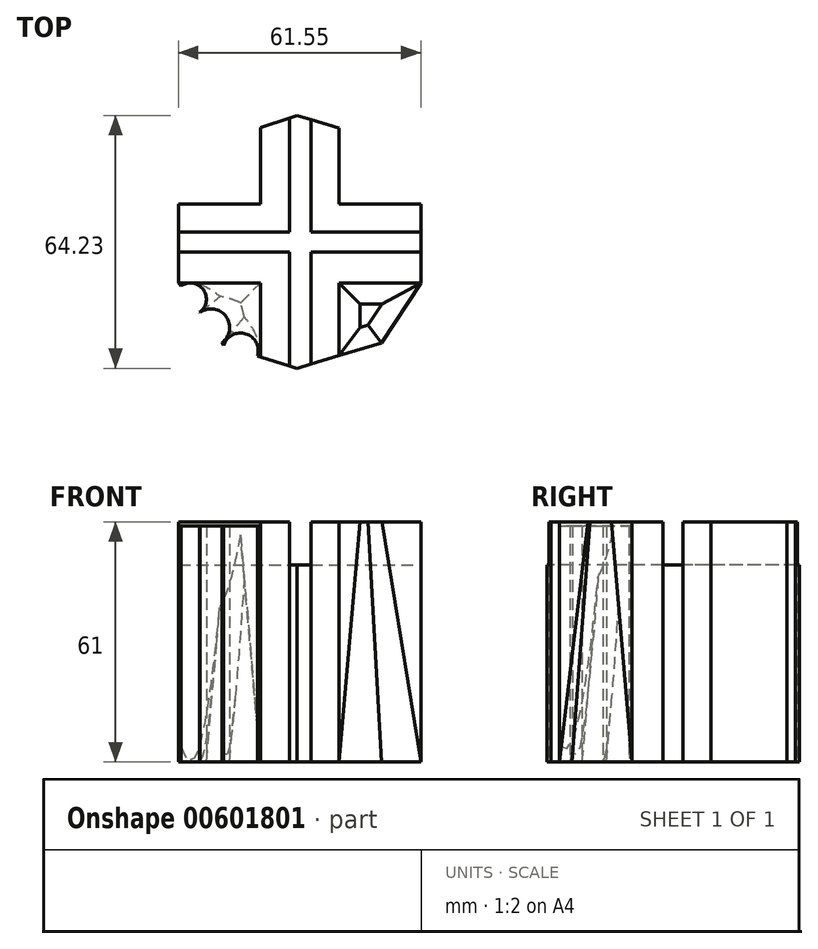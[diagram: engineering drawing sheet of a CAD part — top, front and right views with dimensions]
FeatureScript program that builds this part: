
annotation { "Feature Type Name" : "Feature", "Feature Type Description" : "" }
export const myFeature = defineFeature(function(context is Context, id is Id, definition is map)
    precondition{}
    {
        {
            var Q0;
            Q0=qCreatedBy(makeId("Top.planeOp"),FACE);
            var sketch = newSketch(context, id + "F0", { "sketchPlane" : qUnion([Q0])});
            skLineSegment(sketch, "E0.0", {"start": v(-30.78, -10.35) * mm, "end": v(-30.78, 9.65) * mm});
            skLineSegment(sketch, "E0.1", {"start": v(-30.78, 9.65) * mm, "end": v(-19.3, 26.03) * mm});
            skLineSegment(sketch, "E0.2", {"start": v(-19.3, 26.03) * mm, "end": v(-0.71, 32.18) * mm});
            skLineSegment(sketch, "E0.3", {"start": v(-0.71, 32.18) * mm, "end": v(18.71, 26.39) * mm});
            skLineSegment(sketch, "E0.4", {"start": v(18.71, 26.39) * mm, "end": v(30.77, 9.65) * mm});
            skLineSegment(sketch, "E0.5", {"start": v(30.77, 9.65) * mm, "end": v(30.77, -10.35) * mm});
            skLineSegment(sketch, "E0.6", {"start": v(30.77, -10.35) * mm, "end": v(20.71, -25.6) * mm});
            skLineSegment(sketch, "E0.7", {"start": v(20.71, -25.6) * mm, "end": v(-0.7, -32.05) * mm});
            skLineSegment(sketch, "E0.8", {"start": v(-0.7, -32.05) * mm, "end": v(-19.32, -26.2) * mm});
            skLineSegment(sketch, "E0.9", {"start": v(-19.32, -26.2) * mm, "end": v(-30.78, -10.35) * mm});
            skPoint(sketch, "E0.0.midPoint", {"position": v(-30.78, -0.35) * mm});
            skLineSegment(sketch, "E1", {"start": v(-30.78, 9.65) * mm, "end": v(30.77, 9.65) * mm});
            skLineSegment(sketch, "E2", {"start": v(-30.78, -10.35) * mm, "end": v(30.77, -10.35) * mm});
            skLineSegment(sketch, "E3", {"start": v(-10, 29.1) * mm, "end": v(-10, -29.12) * mm});
            skLineSegment(sketch, "E4", {"start": v(10, 28.98) * mm, "end": v(10, -28.83) * mm});
            skArc(sketch, "E5", {"start": v(-19.32, -26.2) * mm, "mid": v(-13.7, -23.27) * mm, "end": v(-10.77, -28.88) * mm});
            skLineSegment(sketch, "E6", {"start": v(-30.78, 2.54) * mm, "end": v(30.77, 2.54) * mm});
            skLineSegment(sketch, "E7", {"start": v(-2.54, 31.62) * mm, "end": v(-2.54, -31.47) * mm});
            skLineSegment(sketch, "E8", {"start": v(-30.78, -2.54) * mm, "end": v(30.77, -2.54) * mm});
            skLineSegment(sketch, "E9", {"start": v(2.82, 31.13) * mm, "end": v(2.82, -30.99) * mm});
            skArc(sketch, "E10", {"start": v(-25.37, -17.83) * mm, "mid": v(-18.72, -18.9) * mm, "end": v(-19.79, -25.54) * mm});
            skArc(sketch, "E11", {"start": v(-30.2, -11.16) * mm, "mid": v(-24.49, -12.08) * mm, "end": v(-25.4, -17.78) * mm});
            skLineSegment(sketch, "E12", {"start": v(0, 0) * mm, "end": v(-38.82, 0) * mm, "construction": true});
            skLineSegment(sketch, "E13", {"start": v(0, 0) * mm, "end": v(0, -35.82) * mm, "construction": true});
            skSolve(sketch);
        }
        {
            var Q0;
            {var subQ0=sQuery(id+"F0.wireOp",EDGE,"E6");var subQ1=sQuery(id+"F0.wireOp",EDGE,"E0.0");var subQ2=makeQuery(id+"F0.imprint","INTERSECT",VERTEX,{"derivedFrom":[subQ1,subQ0]});Q0=makeQuery(id+"F0.imprint","IMPRINT",FACE,{"disambiguationData":[TD([[makeQuery(id+"F0.imprint","IMPRINT",EDGE,{"disambiguationData":[TD([[subQ2,1.0]])],"derivedFrom":subQ1}),-1.0]])]});}
            var Q1;
            {var subQ0=sQuery(id+"F0.wireOp",EDGE,"E6");var subQ1=sQuery(id+"F0.wireOp",EDGE,"E4");var subQ2=makeQuery(id+"F0.imprint","INTERSECT",VERTEX,{"derivedFrom":[subQ1,subQ0]});Q1=makeQuery(id+"F0.imprint","IMPRINT",FACE,{"disambiguationData":[TD([[makeQuery(id+"F0.imprint","IMPRINT",EDGE,{"disambiguationData":[TD([[subQ2,-1.0]])],"derivedFrom":subQ1}),-1.0]])]});}
            var Q2;
            {var subQ0=sQuery(id+"F0.wireOp",EDGE,"E6");var subQ1=sQuery(id+"F0.wireOp",EDGE,"E3");var subQ2=makeQuery(id+"F0.imprint","INTERSECT",VERTEX,{"derivedFrom":[subQ1,subQ0]});Q2=makeQuery(id+"F0.imprint","IMPRINT",FACE,{"disambiguationData":[TD([[makeQuery(id+"F0.imprint","IMPRINT",EDGE,{"disambiguationData":[TD([[subQ2,-1.0]])],"derivedFrom":subQ1}),1.0]])]});}
            var Q3;
            {var subQ0=sQuery(id+"F0.wireOp",EDGE,"E6");var subQ1=sQuery(id+"F0.wireOp",EDGE,"E0.5");var subQ2=makeQuery(id+"F0.imprint","INTERSECT",VERTEX,{"derivedFrom":[subQ1,subQ0]});Q3=makeQuery(id+"F0.imprint","IMPRINT",FACE,{"disambiguationData":[TD([[makeQuery(id+"F0.imprint","IMPRINT",EDGE,{"disambiguationData":[TD([[subQ2,-1.0]])],"derivedFrom":subQ1}),-1.0]])]});}
            var Q4;
            {var subQ0=sQuery(id+"F0.wireOp",EDGE,"E7");var subQ1=sQuery(id+"F0.wireOp",EDGE,"E2");var subQ2=makeQuery(id+"F0.imprint","INTERSECT",VERTEX,{"derivedFrom":[subQ1,subQ0]});Q4=makeQuery(id+"F0.imprint","IMPRINT",FACE,{"disambiguationData":[TD([[makeQuery(id+"F0.imprint","IMPRINT",EDGE,{"disambiguationData":[TD([[subQ2,-1.0]])],"derivedFrom":subQ1}),1.0]])]});}
            var Q5;
            {var subQ1=sQuery(id+"F0.wireOp",EDGE,"E0.8");var subQ7=sQuery(id+"F0.wireOp",EDGE,"E0.7");var subQ8=makeQuery(id+"F0.imprint","INTERSECT",VERTEX,{"derivedFrom":[subQ7,subQ1]});Q5=makeQuery(id+"F0.imprint","IMPRINT",FACE,{"disambiguationData":[TD([[makeQuery(id+"F0.imprint","IMPRINT",EDGE,{"disambiguationData":[TD([[subQ8,1.0]])],"derivedFrom":subQ7}),-1.0]])]});}
            var Q6;
            {var subQ0=sQuery(id+"F0.wireOp",EDGE,"E7");var subQ1=sQuery(id+"F0.wireOp",EDGE,"E6");var subQ2=makeQuery(id+"F0.imprint","INTERSECT",VERTEX,{"derivedFrom":[subQ1,subQ0]});Q6=makeQuery(id+"F0.imprint","IMPRINT",FACE,{"disambiguationData":[TD([[makeQuery(id+"F0.imprint","IMPRINT",EDGE,{"disambiguationData":[TD([[subQ2,-1.0]])],"derivedFrom":subQ1}),-1.0]])]});}
            var Q7;
            {var subQ0=sQuery(id+"F0.wireOp",EDGE,"E7");var subQ1=sQuery(id+"F0.wireOp",EDGE,"E1");var subQ2=makeQuery(id+"F0.imprint","INTERSECT",VERTEX,{"derivedFrom":[subQ1,subQ0]});Q7=makeQuery(id+"F0.imprint","IMPRINT",FACE,{"disambiguationData":[TD([[makeQuery(id+"F0.imprint","IMPRINT",EDGE,{"disambiguationData":[TD([[subQ2,-1.0]])],"derivedFrom":subQ1}),-1.0]])]});}
            var Q8;
            {var subQ1=sQuery(id+"F0.wireOp",EDGE,"E0.2");var subQ7=sQuery(id+"F0.wireOp",EDGE,"E0.3");var subQ8=makeQuery(id+"F0.imprint","INTERSECT",VERTEX,{"derivedFrom":[subQ1,subQ7]});Q8=makeQuery(id+"F0.imprint","IMPRINT",FACE,{"disambiguationData":[TD([[makeQuery(id+"F0.imprint","IMPRINT",EDGE,{"disambiguationData":[TD([[subQ8,1.0]])],"derivedFrom":subQ1}),-1.0]])]});}
            extrude(context, id + "F1", {"entities" : qUnion([Q0, Q1, Q2, Q3, Q4, Q5, Q6, Q7, Q8]), "depth" : 50 * mm, "offsetDistance" : 25.4 * mm});
        }
        {
            var Q0;
            {var subQ0=sQuery(id+"F0.wireOp",EDGE,"E5");Q0=makeQuery(id+"F0.imprint","IMPRINT",FACE,{"disambiguationData":[TD([[makeQuery(id+"F0.imprint","IMPRINT",EDGE,{"derivedFrom":subQ0}),-1.0]])]});}
            var Q1;
            {var subQ0=sQuery(id+"F0.wireOp",EDGE,"8J1Gu1ok-NpBy-1UeC-TUCD-iMnJK34ZlI8X");Q1=makeQuery(id+"F0.imprint","IMPRINT",FACE,{"disambiguationData":[TD([[makeQuery(id+"F0.imprint","IMPRINT",EDGE,{"derivedFrom":subQ0}),1.0]])]});}
            var Q2;
            {var subQ3=sQuery(id+"F0.wireOp",EDGE,"6BD9QaSZ-MfpA-ervQ-oZPQ-VnF7IO7oEmAR");Q2=makeQuery(id+"F0.imprint","IMPRINT",FACE,{"disambiguationData":[TD([[makeQuery(id+"F0.imprint","IMPRINT",EDGE,{"derivedFrom":subQ3}),1.0]])]});}
            var Q3;
            {var subQ0=sQuery(id+"F0.wireOp",EDGE,"R5kmCIEs-zIm8-F0Dl-lU4v-e940ahxn7PNQ");Q3=makeQuery(id+"F0.imprint","IMPRINT",FACE,{"disambiguationData":[TD([[makeQuery(id+"F0.imprint","IMPRINT",EDGE,{"derivedFrom":subQ0}),-1.0]])]});}
            var Q4;
            {var subQ0=sQuery(id+"F0.wireOp",EDGE,"idttWpr2-uiHC-CvCA-U4ve-1IFPsbuVsxq5");var subQ1=sQuery(id+"F0.wireOp",EDGE,"E0.7");var subQ2=makeQuery(id+"F0.imprint","INTERSECT",VERTEX,{"derivedFrom":[subQ1,subQ0]});Q4=makeQuery(id+"F0.imprint","IMPRINT",FACE,{"disambiguationData":[TD([[makeQuery(id+"F0.imprint","IMPRINT",EDGE,{"disambiguationData":[TD([[subQ2,-1.0]])],"derivedFrom":subQ0}),-1.0]])]});}
            var Q5;
            {var subQ0=sQuery(id+"F0.wireOp",EDGE,"E0.7");var subQ1=sQuery(id+"F0.wireOp",EDGE,"E0.6");var subQ2=makeQuery(id+"F0.imprint","INTERSECT",VERTEX,{"derivedFrom":[subQ1,subQ0]});Q5=makeQuery(id+"F0.imprint","IMPRINT",FACE,{"disambiguationData":[TD([[makeQuery(id+"F0.imprint","IMPRINT",EDGE,{"disambiguationData":[TD([[subQ2,1.0]])],"derivedFrom":subQ1}),-1.0]])]});}
            var Q6;
            {var subQ0=sQuery(id+"F0.wireOp",EDGE,"LsSGLCJH-y8Pd-D1OG-dUl8-uvv9RzYCwggH");Q6=makeQuery(id+"F0.imprint","IMPRINT",FACE,{"disambiguationData":[TD([[makeQuery(id+"F0.imprint","IMPRINT",EDGE,{"derivedFrom":subQ0}),-1.0]])]});}
            var Q7;
            {var subQ0=sQuery(id+"F0.wireOp",EDGE,"E10");Q7=makeQuery(id+"F0.imprint","IMPRINT",FACE,{"disambiguationData":[TD([[makeQuery(id+"F0.imprint","IMPRINT",EDGE,{"derivedFrom":subQ0}),-1.0]])]});}
            var Q8;
            {var subQ0=sQuery(id+"F0.wireOp",EDGE,"8JpMbAC0-Wz2N-mELW-36Mv-evNqgS5GoXTy");Q8=makeQuery(id+"F0.imprint","IMPRINT",FACE,{"disambiguationData":[TD([[makeQuery(id+"F0.imprint","IMPRINT",EDGE,{"derivedFrom":subQ0}),-1.0]])]});}
            var Q9;
            {var subQ0=sQuery(id+"F0.wireOp",EDGE,"1CsoXElv-MLWL-Tqtn-l8Rl-epqaUMYZco4j");Q9=makeQuery(id+"F0.imprint","IMPRINT",FACE,{"disambiguationData":[TD([[makeQuery(id+"F0.imprint","IMPRINT",EDGE,{"derivedFrom":subQ0}),-1.0]])]});}
            var Q10;
            {var subQ0=sQuery(id+"F0.wireOp",EDGE,"sUfSmvuQ-vnFe-6sdE-vN8x-lg7BoAQECs8Z");Q10=makeQuery(id+"F0.imprint","IMPRINT",FACE,{"disambiguationData":[TD([[makeQuery(id+"F0.imprint","IMPRINT",EDGE,{"derivedFrom":subQ0}),-1.0]])]});}
            var Q11;
            {var subQ0=sQuery(id+"F0.wireOp",EDGE,"E11");Q11=makeQuery(id+"F0.imprint","IMPRINT",FACE,{"disambiguationData":[TD([[makeQuery(id+"F0.imprint","IMPRINT",EDGE,{"derivedFrom":subQ0}),-1.0]])]});}
            var Q12;
            {var subQ0=sQuery(id+"F0.wireOp",EDGE,"Ok3GcKrT-zvgn-Wojc-bRoo-KDMGSw0lIzlH");Q12=makeQuery(id+"F0.imprint","IMPRINT",FACE,{"disambiguationData":[TD([[makeQuery(id+"F0.imprint","IMPRINT",EDGE,{"derivedFrom":subQ0}),-1.0]])]});}
            extrude(context, id + "F2", {"entities" : qUnion([Q0, Q1, Q2, Q3, Q4, Q5, Q6, Q7, Q8, Q9, Q10, Q11, Q12]), "depth" : 61 * mm, "offsetDistance" : 25.4 * mm, "hasDraft" : true, "draftAngle" : 5 * degree, "draftPullDirection" : true});
        }
        {
            var Q0;
            {var subQ5=sQuery(id+"F0.wireOp",EDGE,"gX5pFzFx-FXPJ-6mZQ-lB42-4NN3HQDA0lG3");Q0=makeQuery(id+"F0.imprint","IMPRINT",FACE,{"disambiguationData":[TD([[makeQuery(id+"F0.imprint","IMPRINT",EDGE,{"derivedFrom":subQ5}),-1.0]])]});}
            var Q1;
            {var subQ1=sQuery(id+"F0.wireOp",EDGE,"E0.8");var subQ5=sQuery(id+"F0.wireOp",EDGE,"E3");var subQ6=makeQuery(id+"F0.imprint","INTERSECT",VERTEX,{"derivedFrom":[subQ1,subQ5]});Q1=makeQuery(id+"F0.imprint","IMPRINT",FACE,{"disambiguationData":[TD([[makeQuery(id+"F0.imprint","IMPRINT",EDGE,{"disambiguationData":[TD([[subQ6,-1.0]])],"derivedFrom":subQ1}),-1.0]])]});}
            var Q2;
            {var subQ5=sQuery(id+"F0.wireOp",EDGE,"R5kmCIEs-zIm8-F0Dl-lU4v-e940ahxn7PNQ");Q2=makeQuery(id+"F0.imprint","IMPRINT",FACE,{"disambiguationData":[TD([[makeQuery(id+"F0.imprint","IMPRINT",EDGE,{"derivedFrom":subQ5}),1.0]])]});}
            var Q3;
            {var subQ8=sQuery(id+"F0.wireOp",EDGE,"sUfSmvuQ-vnFe-6sdE-vN8x-lg7BoAQECs8Z");Q3=makeQuery(id+"F0.imprint","IMPRINT",FACE,{"disambiguationData":[TD([[makeQuery(id+"F0.imprint","IMPRINT",EDGE,{"derivedFrom":subQ8}),1.0]])]});}
            var Q4;
            {var subQ4=sQuery(id+"F0.wireOp",EDGE,"oMp6X3SR-dit9-NUgI-edi1-ICxVlqs0Do8b");Q4=makeQuery(id+"F0.imprint","IMPRINT",FACE,{"disambiguationData":[TD([[makeQuery(id+"F0.imprint","IMPRINT",EDGE,{"derivedFrom":subQ4}),1.0]])]});}
            extrude(context, id + "F3", {"entities" : qUnion([Q0, Q1, Q2, Q3, Q4]), "depth" : 60 * mm, "offsetDistance" : 25.4 * mm});
        }
        {
            var Q0;
            {var subQ0=sQuery(id+"F0.wireOp",EDGE,"E2");var subQ5=sQuery(id+"F0.wireOp",EDGE,"E4");var subQ6=makeQuery(id+"F0.imprint","INTERSECT",VERTEX,{"derivedFrom":[subQ0,subQ5]});Q0=makeQuery(id+"F0.imprint","IMPRINT",FACE,{"disambiguationData":[TD([[makeQuery(id+"F0.imprint","IMPRINT",EDGE,{"disambiguationData":[TD([[subQ6,1.0]])],"derivedFrom":subQ5}),1.0]])]});}
            var Q1;
            {var subQ0=sQuery(id+"F0.wireOp",EDGE,"E3");var subQ1=sQuery(id+"F0.wireOp",EDGE,"E2");var subQ2=makeQuery(id+"F0.imprint","INTERSECT",VERTEX,{"derivedFrom":[subQ1,subQ0]});Q1=makeQuery(id+"F0.imprint","IMPRINT",FACE,{"disambiguationData":[TD([[makeQuery(id+"F0.imprint","IMPRINT",EDGE,{"disambiguationData":[TD([[subQ2,-1.0]])],"derivedFrom":subQ1}),1.0]])]});}
            var Q2;
            {var subQ0=sQuery(id+"F0.wireOp",EDGE,"E9");var subQ1=sQuery(id+"F0.wireOp",EDGE,"E2");var subQ2=makeQuery(id+"F0.imprint","INTERSECT",VERTEX,{"derivedFrom":[subQ1,subQ0]});Q2=makeQuery(id+"F0.imprint","IMPRINT",FACE,{"disambiguationData":[TD([[makeQuery(id+"F0.imprint","IMPRINT",EDGE,{"disambiguationData":[TD([[subQ2,-1.0]])],"derivedFrom":subQ1}),1.0]])]});}
            var Q3;
            {var subQ0=sQuery(id+"F0.wireOp",EDGE,"E1");var subQ5=sQuery(id+"F0.wireOp",EDGE,"E4");var subQ6=makeQuery(id+"F0.imprint","INTERSECT",VERTEX,{"derivedFrom":[subQ0,subQ5]});Q3=makeQuery(id+"F0.imprint","IMPRINT",FACE,{"disambiguationData":[TD([[makeQuery(id+"F0.imprint","IMPRINT",EDGE,{"disambiguationData":[TD([[subQ6,-1.0]])],"derivedFrom":subQ5}),1.0]])]});}
            var Q4;
            {var subQ0=sQuery(id+"F0.wireOp",EDGE,"E3");var subQ1=sQuery(id+"F0.wireOp",EDGE,"E1");var subQ2=makeQuery(id+"F0.imprint","INTERSECT",VERTEX,{"derivedFrom":[subQ1,subQ0]});Q4=makeQuery(id+"F0.imprint","IMPRINT",FACE,{"disambiguationData":[TD([[makeQuery(id+"F0.imprint","IMPRINT",EDGE,{"disambiguationData":[TD([[subQ2,-1.0]])],"derivedFrom":subQ1}),-1.0]])]});}
            var Q5;
            {var subQ0=sQuery(id+"F0.wireOp",EDGE,"E9");var subQ1=sQuery(id+"F0.wireOp",EDGE,"E1");var subQ2=makeQuery(id+"F0.imprint","INTERSECT",VERTEX,{"derivedFrom":[subQ1,subQ0]});Q5=makeQuery(id+"F0.imprint","IMPRINT",FACE,{"disambiguationData":[TD([[makeQuery(id+"F0.imprint","IMPRINT",EDGE,{"disambiguationData":[TD([[subQ2,-1.0]])],"derivedFrom":subQ1}),-1.0]])]});}
            var Q6;
            {var subQ0=sQuery(id+"F0.wireOp",EDGE,"E3");var subQ1=sQuery(id+"F0.wireOp",EDGE,"E0.8");var subQ2=makeQuery(id+"F0.imprint","INTERSECT",VERTEX,{"derivedFrom":[subQ1,subQ0]});Q6=makeQuery(id+"F0.imprint","IMPRINT",FACE,{"disambiguationData":[TD([[makeQuery(id+"F0.imprint","IMPRINT",EDGE,{"disambiguationData":[TD([[subQ2,1.0]])],"derivedFrom":subQ1}),-1.0]])]});}
            var Q7;
            {var subQ0=sQuery(id+"F0.wireOp",EDGE,"E4");var subQ1=sQuery(id+"F0.wireOp",EDGE,"E0.3");var subQ2=makeQuery(id+"F0.imprint","INTERSECT",VERTEX,{"derivedFrom":[subQ1,subQ0]});Q7=makeQuery(id+"F0.imprint","IMPRINT",FACE,{"disambiguationData":[TD([[makeQuery(id+"F0.imprint","IMPRINT",EDGE,{"disambiguationData":[TD([[subQ2,1.0]])],"derivedFrom":subQ1}),-1.0]])]});}
            var Q8;
            {var subQ0=sQuery(id+"F0.wireOp",EDGE,"E4");var subQ1=sQuery(id+"F0.wireOp",EDGE,"E0.7");var subQ2=makeQuery(id+"F0.imprint","INTERSECT",VERTEX,{"derivedFrom":[subQ1,subQ0]});Q8=makeQuery(id+"F0.imprint","IMPRINT",FACE,{"disambiguationData":[TD([[makeQuery(id+"F0.imprint","IMPRINT",EDGE,{"disambiguationData":[TD([[subQ2,-1.0]])],"derivedFrom":subQ1}),-1.0]])]});}
            var Q9;
            {var subQ0=sQuery(id+"F0.wireOp",EDGE,"E1");var subQ5=sQuery(id+"F0.wireOp",EDGE,"E3");var subQ6=makeQuery(id+"F0.imprint","INTERSECT",VERTEX,{"derivedFrom":[subQ0,subQ5]});Q9=makeQuery(id+"F0.imprint","IMPRINT",FACE,{"disambiguationData":[TD([[makeQuery(id+"F0.imprint","IMPRINT",EDGE,{"disambiguationData":[TD([[subQ6,-1.0]])],"derivedFrom":subQ5}),-1.0]])]});}
            var Q10;
            {var subQ0=sQuery(id+"F0.wireOp",EDGE,"E3");var subQ1=sQuery(id+"F0.wireOp",EDGE,"E0.2");var subQ2=makeQuery(id+"F0.imprint","INTERSECT",VERTEX,{"derivedFrom":[subQ1,subQ0]});Q10=makeQuery(id+"F0.imprint","IMPRINT",FACE,{"disambiguationData":[TD([[makeQuery(id+"F0.imprint","IMPRINT",EDGE,{"disambiguationData":[TD([[subQ2,-1.0]])],"derivedFrom":subQ1}),-1.0]])]});}
            var Q11;
            {var subQ0=sQuery(id+"F0.wireOp",EDGE,"E2");var subQ5=sQuery(id+"F0.wireOp",EDGE,"E3");var subQ6=makeQuery(id+"F0.imprint","INTERSECT",VERTEX,{"derivedFrom":[subQ0,subQ5]});Q11=makeQuery(id+"F0.imprint","IMPRINT",FACE,{"disambiguationData":[TD([[makeQuery(id+"F0.imprint","IMPRINT",EDGE,{"disambiguationData":[TD([[subQ6,1.0]])],"derivedFrom":subQ5}),-1.0]])]});}
            extrude(context, id + "F4", {"entities" : qUnion([Q0, Q1, Q2, Q3, Q4, Q5, Q6, Q7, Q8, Q9, Q10, Q11]), "depth" : 61 * mm, "offsetDistance" : 25.4 * mm});
        }
    });
